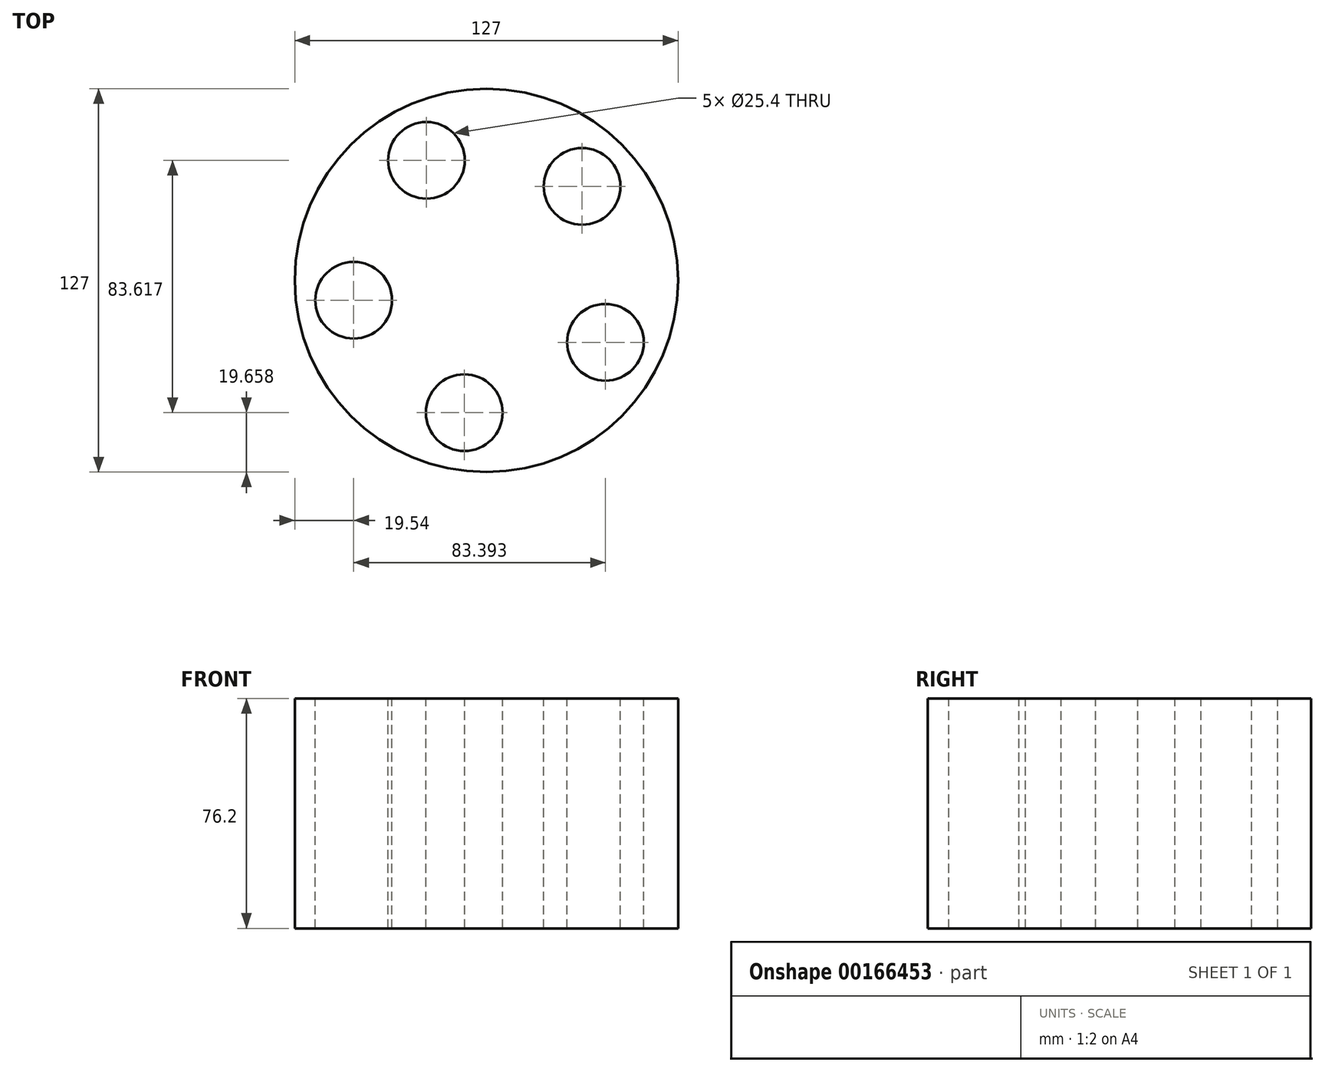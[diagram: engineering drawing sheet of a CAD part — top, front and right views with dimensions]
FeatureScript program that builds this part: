
annotation { "Feature Type Name" : "Feature", "Feature Type Description" : "" }
export const myFeature = defineFeature(function(context is Context, id is Id, definition is map)
    precondition{}
    {
        {
            var Q0;
            Q0=qCreatedBy(makeId("Top.planeOp"),FACE);
            var sketch = newSketch(context, id + "F0", { "sketchPlane" : qUnion([Q0])});
            skCircle(sketch, "E0", {"center": v(0, 0) * mm, "radius": 63.5 * mm});
            skSolve(sketch);
        }
        {
            var Q0;
            Q0 = qSketchRegion(id + "F0", true);
            extrude(context, id + "F1", {"entities" : qUnion([Q0]), "depth" : 76.2 * mm});
        }
        {
            var Q0;
            Q0=makeQuery(id+"F1.opExtrude","CAP_FACE",FACE,{"disambiguationData":[OSD([sQuery(id+"F0.wireOp",EDGE,"E0")])],"isStart":false});
            var sketch = newSketch(context, id + "F2", { "sketchPlane" : qUnion([Q0])});
            skCircle(sketch, "E1.cCircle", {"center": v(0, 0) * mm, "radius": 44.45 * mm, "construction": true});
            skLineSegment(sketch, "E1.0", {"start": v(39.43, -20.51) * mm, "end": v(-7.33, -43.84) * mm, "construction": true});
            skLineSegment(sketch, "E1.1", {"start": v(-7.33, -43.84) * mm, "end": v(-43.96, -6.58) * mm, "construction": true});
            skLineSegment(sketch, "E1.2", {"start": v(-43.96, -6.58) * mm, "end": v(-19.84, 39.77) * mm, "construction": true});
            skLineSegment(sketch, "E1.3", {"start": v(-19.84, 39.77) * mm, "end": v(31.7, 31.16) * mm, "construction": true});
            skLineSegment(sketch, "E1.4", {"start": v(31.7, 31.16) * mm, "end": v(39.43, -20.51) * mm, "construction": true});
            skCircle(sketch, "E2", {"center": v(-19.84, 39.77) * mm, "radius": 12.7 * mm});
            skCircle(sketch, "E3", {"center": v(31.7, 31.16) * mm, "radius": 12.7 * mm});
            skCircle(sketch, "E4", {"center": v(39.43, -20.51) * mm, "radius": 12.7 * mm});
            skCircle(sketch, "E5", {"center": v(-7.33, -43.84) * mm, "radius": 12.7 * mm});
            skCircle(sketch, "E6", {"center": v(-43.96, -6.58) * mm, "radius": 12.7 * mm});
            skSolve(sketch);
        }
        {
            var Q0;
            Q0 = qSketchRegion(id + "F2", true);
            var Q1;
            Q1 = qConstructionFilter(qBodyType(qCreatedBy(id + "F2" ,EDGE), BodyType.WIRE), ConstructionObject.NO);
            extrude(context, id + "F3", {"entities" : qUnion([Q0]), "operationType" : NewBodyOperationType.REMOVE, "surfaceEntities" : qUnion([Q1]), "endBound" : BoundingType.THROUGH_ALL, "oppositeDirection" : true, "depth" : 25.4 * mm});
        }
    });
